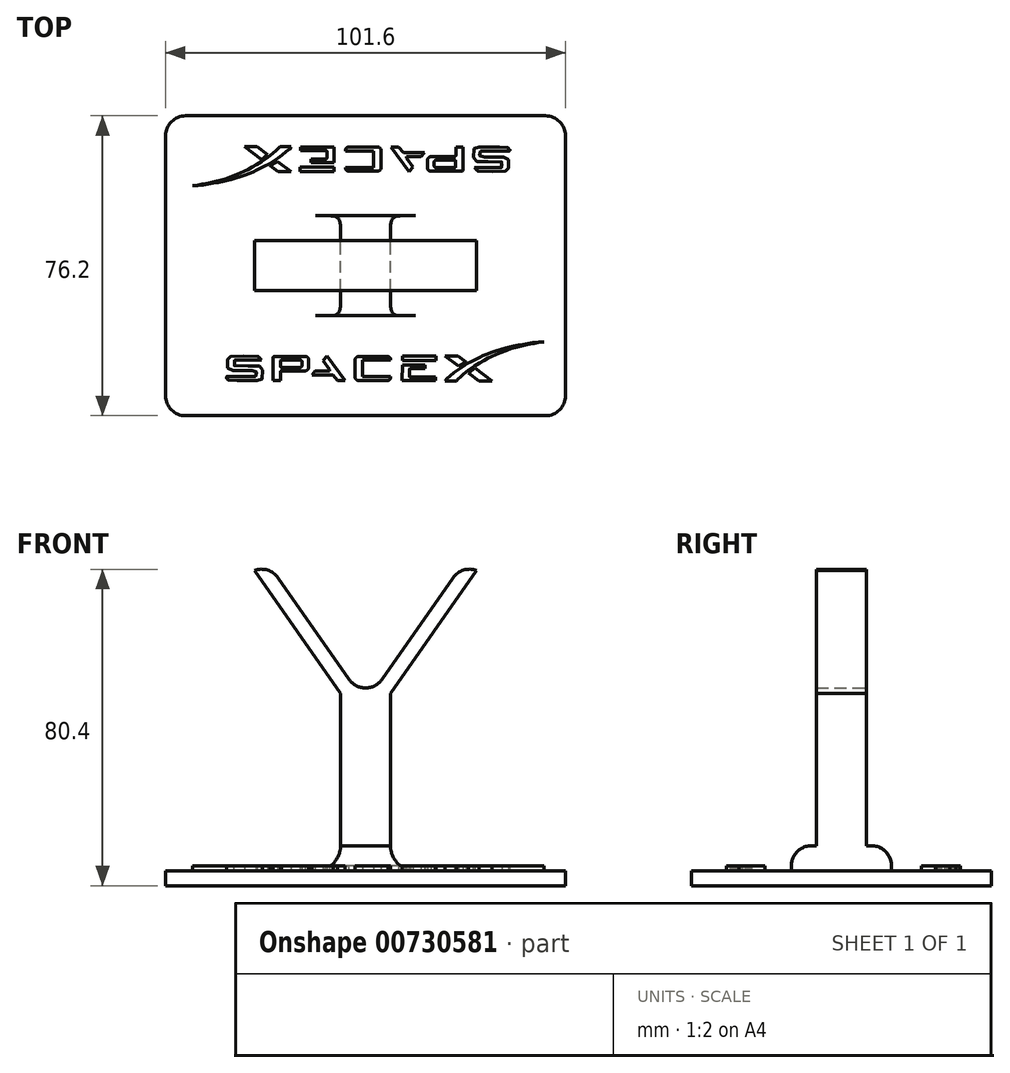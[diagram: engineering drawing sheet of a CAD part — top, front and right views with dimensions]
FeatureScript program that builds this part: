
annotation { "Feature Type Name" : "Feature", "Feature Type Description" : "" }
export const myFeature = defineFeature(function(context is Context, id is Id, definition is map)
    precondition{}
    {
        {
            var Q0;
            Q0=qCreatedBy(makeId("Front.planeOp"),FACE);
            var sketch = newSketch(context, id + "F0", { "sketchPlane" : qUnion([Q0])});
            skLineSegment(sketch, "E0.left", {"start": v(-20.93, 31.6) * mm, "end": v(-20.93, 73.8) * mm});
            skLineSegment(sketch, "E0.right", {"start": v(-33.63, 31.6) * mm, "end": v(-33.63, 73.8) * mm});
            skArc(sketch, "E1.filletArc", {"start": v(-39.98, 25.26) * mm, "mid": v(-35.5, 27.12) * mm, "end": v(-33.63, 31.6) * mm});
            skLineSegment(sketch, "E2", {"start": v(23.52, 25.26) * mm, "end": v(-14.58, 25.26) * mm});
            skArc(sketch, "E3.filletArc", {"start": v(-20.93, 31.6) * mm, "mid": v(-19.07, 27.12) * mm, "end": v(-14.58, 25.26) * mm});
            skLineSegment(sketch, "E4", {"start": v(-33.63, 70.32) * mm, "end": v(-55.49, 101.53) * mm});
            skLineSegment(sketch, "E5", {"start": v(-78.08, 21.45) * mm, "end": v(-78.08, 25.26) * mm});
            skLineSegment(sketch, "E6", {"start": v(23.52, 21.45) * mm, "end": v(23.52, 25.26) * mm});
            skLineSegment(sketch, "E7", {"start": v(-78.08, 25.26) * mm, "end": v(-39.98, 25.26) * mm});
            skLineSegment(sketch, "E8", {"start": v(-78.08, 21.45) * mm, "end": v(23.52, 21.45) * mm});
            skLineSegment(sketch, "E9", {"start": v(-55.49, 101.53) * mm, "end": v(-52.37, 103.71) * mm});
            skLineSegment(sketch, "E10", {"start": v(-52.37, 103.71) * mm, "end": v(-27.28, 67.9) * mm});
            skLineSegment(sketch, "E11.MirrorCS", {"start": v(-2.2, 103.71) * mm, "end": v(-27.28, 67.9) * mm});
            skLineSegment(sketch, "E12.MirrorCS", {"start": v(0.92, 101.53) * mm, "end": v(-2.2, 103.71) * mm});
            skLineSegment(sketch, "E13.MirrorCS", {"start": v(-20.93, 70.32) * mm, "end": v(0.92, 101.53) * mm});
            skLineSegment(sketch, "E14", {"start": v(-33.63, 62.87) * mm, "end": v(-20.93, 62.87) * mm});
            skLineSegment(sketch, "E15", {"start": v(-39.98, 25.26) * mm, "end": v(-14.58, 25.26) * mm});
            skLineSegment(sketch, "E16", {"start": v(-33.63, 31.6) * mm, "end": v(-20.93, 31.6) * mm});
            skSolve(sketch);
        }
        {
            var Q0;
            {var subQ1=sQuery(id+"F0.wireOp",EDGE,"E5");Q0=makeQuery(id+"F0.imprint","IMPRINT",FACE,{"disambiguationData":[TD([[makeQuery(id+"F0.imprint","IMPRINT",EDGE,{"derivedFrom":subQ1}),-1.0]])]});}
            var Q1;
            {var subQ6=sQuery(id+"F0.wireOp",EDGE,"E2");Q1=makeQuery(id+"F0.imprint","IMPRINT",FACE,{"disambiguationData":[TD([[makeQuery(id+"F0.imprint","IMPRINT",EDGE,{"derivedFrom":subQ6}),1.0]])]});}
            extrude(context, id + "F1", {"entities" : qUnion([Q0, Q1]), "depth" : 76.2 * mm, "offsetDistance" : 25.4 * mm, "symmetric" : true});
        }
        {
            var Q0;
            Q0=makeQuery(id+"F0.imprint","IMPRINT",FACE,{"disambiguationData":[TD([[makeQuery(id+"F0.imprint","IMPRINT",EDGE,{"derivedFrom":sQuery(id+"F0.wireOp",EDGE,"E1.filletArc")}),-1.0]])]});
            extrude(context, id + "F2", {"entities" : qUnion([Q0]), "operationType" : NewBodyOperationType.ADD, "depth" : 25.4 * mm, "offsetDistance" : 25.4 * mm, "symmetric" : true});
        }
        {
            var Q0;
            {var subQ2=sQuery(id+"F0.wireOp",EDGE,"E14");Q0=makeQuery(id+"F0.imprint","IMPRINT",FACE,{"disambiguationData":[TD([[makeQuery(id+"F0.imprint","IMPRINT",EDGE,{"derivedFrom":subQ2}),-1.0]])]});}
            var Q1;
            {var subQ3=sQuery(id+"F0.wireOp",EDGE,"E4");Q1=makeQuery(id+"F0.imprint","IMPRINT",FACE,{"disambiguationData":[TD([[makeQuery(id+"F0.imprint","IMPRINT",EDGE,{"derivedFrom":subQ3}),-1.0]])]});}
            extrude(context, id + "F3", {"entities" : qUnion([Q0, Q1]), "operationType" : NewBodyOperationType.ADD, "depth" : 12.7 * mm, "offsetDistance" : 25.4 * mm, "symmetric" : true});
        }
        {
            var Q0;
            Q0=makeQuery(id+"F2.opExtrude","CAP_EDGE",EDGE,{"disambiguationData":[OSD([sQuery(id+"F0.wireOp",EDGE,"E16")])],"isStart":false});
            var Q1;
            Q1=makeQuery(id+"F2.opExtrude","CAP_EDGE",EDGE,{"disambiguationData":[OSD([sQuery(id+"F0.wireOp",EDGE,"E16")])],"isStart":true});
            fillet(context, id + "F4", {"entities" : qUnion([Q0, Q1]), "radius" : 5.08 * mm, "tangentPropagation" : true, "allowEdgeOverflow" : false});
        }
        {
            var Q0;
            Q0=makeQuery(id+"F1.opExtrude","CAP_EDGE",EDGE,{"disambiguationData":[OSD([sQuery(id+"F0.wireOp",EDGE,"E6")])],"isStart":false});
            var Q1;
            Q1=makeQuery(id+"F1.opExtrude","CAP_EDGE",EDGE,{"disambiguationData":[OSD([sQuery(id+"F0.wireOp",EDGE,"E6")])],"isStart":true});
            var Q2;
            Q2=makeQuery(id+"F1.opExtrude","CAP_EDGE",EDGE,{"disambiguationData":[OSD([sQuery(id+"F0.wireOp",EDGE,"E5")])],"isStart":true});
            var Q3;
            Q3=makeQuery(id+"F1.opExtrude","CAP_EDGE",EDGE,{"disambiguationData":[OSD([sQuery(id+"F0.wireOp",EDGE,"E5")])],"isStart":false});
            var Q4;
            Q4=makeQuery(id+"F3.opExtrude","SWEPT_EDGE",EDGE,{"disambiguationData":[OSD([sQuery(id+"F0.wireOp",EDGE,"E11.MirrorCS"),sQuery(id+"F0.wireOp",EDGE,"E12.MirrorCS")])]});
            var Q5;
            Q5=makeQuery(id+"F3.opExtrude","SWEPT_EDGE",EDGE,{"disambiguationData":[OSD([sQuery(id+"F0.wireOp",EDGE,"E9"),sQuery(id+"F0.wireOp",EDGE,"E10")])]});
            var Q6;
            Q6=makeQuery(id+"F3.opExtrude","SWEPT_EDGE",EDGE,{"disambiguationData":[OSD([sQuery(id+"F0.wireOp",EDGE,"E10"),sQuery(id+"F0.wireOp",EDGE,"E11.MirrorCS")])]});
            fillet(context, id + "F5", {"entities" : qUnion([Q0, Q1, Q2, Q3, Q4, Q5, Q6]), "radius" : 5.08 * mm, "tangentPropagation" : true, "allowEdgeOverflow" : false});
        }
        {
            var Q0;
            Q0=makeQuery(id+"F1.opExtrude","SWEPT_BODY",BODY,{"disambiguationData":[OSD([sQuery(id+"F0.wireOp",EDGE,"E2"),sQuery(id+"F0.wireOp",EDGE,"E5"),sQuery(id+"F0.wireOp",EDGE,"E6"),sQuery(id+"F0.wireOp",EDGE,"E7"),sQuery(id+"F0.wireOp",EDGE,"E8"),sQuery(id+"F0.wireOp",EDGE,"E15")])]});
            transform(context, id + "F6", {"entities" : qUnion([Q0]), "transformType" : TransformType.TRANSLATION_3D, "dx" : 0 * mm, "dy" : 0 * mm, "dz" : -22.1 * mm, "makeCopy" : false});
        }
        {
            var Q0;
            Q0=qCreatedBy(makeId("Top.planeOp"),FACE);
            var sketch = newSketch(context, id + "F7", { "sketchPlane" : qUnion([Q0])});
            skFitSpline(sketch, "E17", {"points": [v(-53.7, -23.92) * mm, v(-53.67, -23.65) * mm, v(-54.32, -23.13) * mm, v(-55.17, -23) * mm, v(-61.33, -23.02) * mm, v(-61.6, -23.06) * mm, v(-61.93, -23.15) * mm, v(-62.22, -23.56) * mm, v(-62.38, -24.03) * mm, v(-62.32, -25.77) * mm, v(-62.18, -26.17) * mm, v(-61.56, -26.5) * mm, v(-59.98, -26.56) * mm, v(-57.92, -26.56) * mm, v(-56.25, -26.56) * mm, v(-55.43, -26.6) * mm, v(-55.05, -26.71) * mm, v(-55, -27.47) * mm, v(-55, -28) * mm, v(-55.23, -28.12) * mm, v(-55.77, -28.13) * mm, v(-62.38, -28.13) * mm, v(-62.6, -28.18) * mm, v(-62.64, -28.45) * mm, v(-62.48, -28.76) * mm, v(-61.97, -29.1) * mm, v(-61.31, -29.16) * mm, v(-54.45, -29.16) * mm, v(-54.07, -29.11) * mm, v(-53.64, -28.84) * mm, v(-53.44, -28.23) * mm, v(-53.44, -26.31) * mm, v(-53.63, -25.89) * mm, v(-54.23, -25.5) * mm, v(-55.29, -25.42) * mm, v(-60.36, -25.4) * mm, v(-60.65, -25.3) * mm, v(-60.72, -24.19) * mm, v(-60.45, -24) * mm, v(-54.19, -23.94) * mm, v(-53.88, -23.9) * mm, v(-53.7, -23.92) * mm]});
            skLineSegment(sketch, "E18", {"start": v(-50.52, -23.04) * mm, "end": v(-42.6, -23.04) * mm});
            skLineSegment(sketch, "E19", {"start": v(-48.66, -23.95) * mm, "end": v(-43.86, -23.95) * mm});
            skLineSegment(sketch, "E20", {"start": v(-43.44, -24.28) * mm, "end": v(-43.44, -25.47) * mm});
            skLineSegment(sketch, "E21", {"start": v(-48.68, -25.82) * mm, "end": v(-43.94, -25.82) * mm});
            skLineSegment(sketch, "E22", {"start": v(-48.88, -24.14) * mm, "end": v(-48.88, -25.62) * mm});
            skLineSegment(sketch, "E23", {"start": v(-50.74, -23.29) * mm, "end": v(-50.74, -29.17) * mm});
            skLineSegment(sketch, "E24", {"start": v(-50.74, -29.17) * mm, "end": v(-48.91, -29.17) * mm});
            skLineSegment(sketch, "E25", {"start": v(-48.91, -29.17) * mm, "end": v(-48.91, -26.97) * mm});
            skLineSegment(sketch, "E26", {"start": v(-48.62, -26.7) * mm, "end": v(-42.66, -26.7) * mm});
            skLineSegment(sketch, "E27", {"start": v(-41.74, -23.79) * mm, "end": v(-41.74, -25.97) * mm});
            skFitSpline(sketch, "E28", {"points": [v(-42.6, -23.04) * mm, v(-42.1, -23.18) * mm, v(-41.74, -23.79) * mm], "startDerivative": vector(1.29, -0.1) * mm, "endDerivative": vector(0.06, -1.49) * mm});
            skArc(sketch, "E29", {"start": v(-48.66, -23.95) * mm, "mid": v(-48.8, -24) * mm, "end": v(-48.88, -24.14) * mm});
            skArc(sketch, "E30", {"start": v(-43.44, -24.28) * mm, "mid": v(-43.6, -24.05) * mm, "end": v(-43.86, -23.95) * mm});
            skArc(sketch, "E31", {"start": v(-43.94, -25.82) * mm, "mid": v(-43.64, -25.72) * mm, "end": v(-43.44, -25.47) * mm});
            skArc(sketch, "E32", {"start": v(-48.88, -25.62) * mm, "mid": v(-48.82, -25.76) * mm, "end": v(-48.68, -25.82) * mm});
            skArc(sketch, "E33", {"start": v(-48.62, -26.7) * mm, "mid": v(-48.83, -26.78) * mm, "end": v(-48.91, -26.97) * mm});
            skArc(sketch, "E34", {"start": v(-50.52, -23.04) * mm, "mid": v(-50.68, -23.12) * mm, "end": v(-50.74, -23.29) * mm});
            skArc(sketch, "E35", {"start": v(-42.66, -26.7) * mm, "mid": v(-42.07, -26.5) * mm, "end": v(-41.74, -25.97) * mm});
            skLineSegment(sketch, "E36", {"start": v(-40.1, -26.79) * mm, "end": v(-36.45, -26.79) * mm});
            skLineSegment(sketch, "E37", {"start": v(-40.93, -27.8) * mm, "end": v(-35.58, -27.8) * mm});
            skLineSegment(sketch, "E38", {"start": v(-34.41, -29.2) * mm, "end": v(-32.43, -29.2) * mm});
            skLineSegment(sketch, "E39", {"start": v(-36.45, -26.79) * mm, "end": v(-36.45, -26.32) * mm});
            skLineSegment(sketch, "E40", {"start": v(-36.45, -26.32) * mm, "end": v(-38.08, -24.1) * mm});
            skLineSegment(sketch, "E41", {"start": v(-38.08, -24.1) * mm, "end": v(-37.07, -22.88) * mm});
            skLineSegment(sketch, "E42", {"start": v(-37.07, -22.88) * mm, "end": v(-32.43, -29.2) * mm});
            skLineSegment(sketch, "E43", {"start": v(-40.93, -27.8) * mm, "end": v(-40.1, -26.79) * mm});
            skLineSegment(sketch, "E44", {"start": v(-35.58, -27.8) * mm, "end": v(-34.41, -29.2) * mm});
            skLineSegment(sketch, "E45", {"start": v(-28.05, -23.98) * mm, "end": v(-28.05, -28.08) * mm});
            skLineSegment(sketch, "E46", {"start": v(-28.05, -28.08) * mm, "end": v(-20.92, -28.08) * mm});
            skLineSegment(sketch, "E47", {"start": v(-28.05, -23.98) * mm, "end": v(-20.93, -23.98) * mm});
            skLineSegment(sketch, "E48", {"start": v(-29.95, -23.98) * mm, "end": v(-29.95, -28.17) * mm});
            skLineSegment(sketch, "E49", {"start": v(-29.03, -23.05) * mm, "end": v(-21.68, -23.05) * mm});
            skLineSegment(sketch, "E50", {"start": v(-28.99, -29.18) * mm, "end": v(-21.6, -29.18) * mm});
            skArc(sketch, "E51", {"start": v(-29.03, -23.05) * mm, "mid": v(-29.68, -23.32) * mm, "end": v(-29.95, -23.98) * mm});
            skArc(sketch, "E52", {"start": v(-20.93, -23.98) * mm, "mid": v(-21.08, -23.34) * mm, "end": v(-21.68, -23.05) * mm});
            skArc(sketch, "E53", {"start": v(-21.6, -29.18) * mm, "mid": v(-21.04, -28.77) * mm, "end": v(-20.92, -28.08) * mm});
            skArc(sketch, "E54", {"start": v(-29.95, -28.17) * mm, "mid": v(-29.68, -28.88) * mm, "end": v(-28.99, -29.18) * mm});
            skLineSegment(sketch, "E55", {"start": v(-17.93, -22.97) * mm, "end": v(-17.93, -24.06) * mm});
            skLineSegment(sketch, "E56", {"start": v(-17.93, -24.06) * mm, "end": v(-9.36, -24.06) * mm});
            skLineSegment(sketch, "E57", {"start": v(-9.36, -24.06) * mm, "end": v(-9.36, -23) * mm});
            skLineSegment(sketch, "E58", {"start": v(-9.36, -23) * mm, "end": v(-17.93, -22.97) * mm});
            skLineSegment(sketch, "E59", {"start": v(-17.93, -25.16) * mm, "end": v(-12.2, -25.16) * mm});
            skLineSegment(sketch, "E60", {"start": v(-12.2, -25.16) * mm, "end": v(-12.2, -26.1) * mm});
            skLineSegment(sketch, "E61", {"start": v(-12.2, -26.1) * mm, "end": v(-15.84, -26.1) * mm});
            skLineSegment(sketch, "E62", {"start": v(-16.16, -26.36) * mm, "end": v(-16.16, -28.1) * mm});
            skLineSegment(sketch, "E63", {"start": v(-15.85, -28.28) * mm, "end": v(-9.49, -28.28) * mm});
            skLineSegment(sketch, "E64", {"start": v(-9.49, -28.28) * mm, "end": v(-9.49, -29.2) * mm});
            skLineSegment(sketch, "E65", {"start": v(-9.49, -29.2) * mm, "end": v(-17.95, -29.2) * mm});
            skLineSegment(sketch, "E66", {"start": v(-17.95, -29.2) * mm, "end": v(-17.93, -25.16) * mm});
            skArc(sketch, "E67", {"start": v(-15.84, -26.1) * mm, "mid": v(-16.05, -26.17) * mm, "end": v(-16.16, -26.36) * mm});
            skArc(sketch, "E68", {"start": v(-16.16, -28.1) * mm, "mid": v(-16.04, -28.25) * mm, "end": v(-15.85, -28.28) * mm});
            skLineSegment(sketch, "E69", {"start": v(-3.63, -25.47) * mm, "end": v(-7.06, -22.9) * mm});
            skLineSegment(sketch, "E70", {"start": v(-7.06, -22.9) * mm, "end": v(-3.82, -22.9) * mm});
            skLineSegment(sketch, "E71", {"start": v(-3.82, -22.9) * mm, "end": v(-1.73, -24.46) * mm});
            skLineSegment(sketch, "E72", {"start": v(-1.73, -24.46) * mm, "end": v(-3.63, -25.47) * mm});
            skLineSegment(sketch, "E73", {"start": v(-1.12, -27.26) * mm, "end": v(1.55, -29.22) * mm});
            skLineSegment(sketch, "E74", {"start": v(1.55, -29.22) * mm, "end": v(4.8, -29.22) * mm});
            skLineSegment(sketch, "E75", {"start": v(4.8, -29.22) * mm, "end": v(0.47, -26.03) * mm});
            skLineSegment(sketch, "E76", {"start": v(0.47, -26.03) * mm, "end": v(-1.12, -27.26) * mm});
            skFitSpline(sketch, "E77", {"points": [v(-4.23, -29.23) * mm, v(-3.52, -28.52) * mm, v(-2.4, -27.5) * mm, v(0.11, -25.65) * mm, v(3.4, -23.71) * mm, v(5.5, -22.67) * mm, v(9.22, -21.24) * mm, v(11.62, -20.56) * mm, v(13.9, -20.02) * mm, v(15.25, -19.77) * mm, v(17.22, -19.44) * mm, v(18.02, -19.37) * mm], "startDerivative": vector(10.87, 11.15) * mm, "endDerivative": vector(12.33, 0.65) * mm});
            skLineSegment(sketch, "E78", {"start": v(-4.23, -29.23) * mm, "end": v(-7.08, -29.23) * mm});
            skFitSpline(sketch, "E79", {"points": [v(-7.08, -29.23) * mm, v(-6.81, -28.85) * mm, v(-6.22, -28.29) * mm, v(-5.06, -27.3) * mm, v(-3.56, -26.22) * mm, v(-2.03, -25.2) * mm, v(-0.72, -24.47) * mm, v(0.48, -23.87) * mm, v(1.64, -23.27) * mm, v(2.58, -22.85) * mm, v(3.7, -22.38) * mm, v(4.77, -21.96) * mm, v(6.18, -21.52) * mm, v(7.73, -21.07) * mm, v(8.94, -20.77) * mm, v(10.06, -20.5) * mm, v(11.42, -20.22) * mm, v(12.81, -19.93) * mm, v(14.55, -19.66) * mm, v(16.14, -19.45) * mm, v(18.02, -19.37) * mm], "startDerivative": vector(8, 12.9) * mm, "endDerivative": vector(32.76, 0.76) * mm});
            skFitSpline(sketch, "E80", {"points": [v(0.43, 24.93) * mm, v(0.4, 24.65) * mm, v(1.05, 24.14) * mm, v(1.9, 24) * mm, v(8.06, 24.02) * mm, v(8.34, 24.07) * mm, v(8.66, 24.15) * mm, v(8.95, 24.56) * mm, v(9.11, 25.03) * mm, v(9.05, 26.78) * mm, v(8.9, 27.17) * mm, v(8.3, 27.51) * mm, v(6.7, 27.57) * mm, v(4.66, 27.57) * mm, v(2.98, 27.57) * mm, v(2.16, 27.6) * mm, v(1.78, 27.72) * mm, v(1.72, 28.48) * mm, v(1.72, 29) * mm, v(1.96, 29.12) * mm, v(2.5, 29.14) * mm, v(9.11, 29.14) * mm, v(9.33, 29.18) * mm, v(9.38, 29.46) * mm, v(9.22, 29.77) * mm, v(8.7, 30.1) * mm, v(8.04, 30.16) * mm, v(1.18, 30.16) * mm, v(0.8, 30.12) * mm, v(0.37, 29.84) * mm, v(0.17, 29.24) * mm, v(0.17, 27.32) * mm, v(0.36, 26.9) * mm, v(0.96, 26.5) * mm, v(2.02, 26.43) * mm, v(7.09, 26.41) * mm, v(7.38, 26.3) * mm, v(7.46, 25.2) * mm, v(7.18, 25) * mm, v(0.92, 24.95) * mm, v(0.6, 24.92) * mm, v(0.43, 24.93) * mm]});
            skLineSegment(sketch, "E81", {"start": v(-2.75, 24.05) * mm, "end": v(-10.67, 24.05) * mm});
            skLineSegment(sketch, "E82", {"start": v(-4.61, 24.96) * mm, "end": v(-9.4, 24.96) * mm});
            skLineSegment(sketch, "E83", {"start": v(-9.82, 25.29) * mm, "end": v(-9.82, 26.48) * mm});
            skLineSegment(sketch, "E84", {"start": v(-4.6, 26.82) * mm, "end": v(-9.33, 26.82) * mm});
            skLineSegment(sketch, "E85", {"start": v(-4.39, 25.15) * mm, "end": v(-4.39, 26.62) * mm});
            skLineSegment(sketch, "E86", {"start": v(-2.53, 24.3) * mm, "end": v(-2.53, 30.18) * mm});
            skLineSegment(sketch, "E87", {"start": v(-2.53, 30.18) * mm, "end": v(-4.36, 30.18) * mm});
            skLineSegment(sketch, "E88", {"start": v(-4.36, 30.18) * mm, "end": v(-4.36, 27.98) * mm});
            skLineSegment(sketch, "E89", {"start": v(-4.64, 27.71) * mm, "end": v(-10.6, 27.71) * mm});
            skLineSegment(sketch, "E90", {"start": v(-11.52, 24.8) * mm, "end": v(-11.52, 26.98) * mm});
            skFitSpline(sketch, "E91", {"points": [v(-10.67, 24.05) * mm, v(-11.17, 24.19) * mm, v(-11.52, 24.8) * mm], "startDerivative": vector(-1.29, 0.1) * mm, "endDerivative": vector(-0.06, 1.49) * mm});
            skArc(sketch, "E92", {"start": v(-4.61, 24.96) * mm, "mid": v(-4.46, 25.01) * mm, "end": v(-4.39, 25.15) * mm});
            skArc(sketch, "E93", {"start": v(-9.82, 25.29) * mm, "mid": v(-9.67, 25.05) * mm, "end": v(-9.4, 24.96) * mm});
            skArc(sketch, "E94", {"start": v(-9.33, 26.82) * mm, "mid": v(-9.63, 26.73) * mm, "end": v(-9.82, 26.48) * mm});
            skArc(sketch, "E95", {"start": v(-4.39, 26.62) * mm, "mid": v(-4.45, 26.77) * mm, "end": v(-4.6, 26.82) * mm});
            skArc(sketch, "E96", {"start": v(-4.64, 27.71) * mm, "mid": v(-4.44, 27.78) * mm, "end": v(-4.36, 27.98) * mm});
            skArc(sketch, "E97", {"start": v(-2.75, 24.05) * mm, "mid": v(-2.58, 24.12) * mm, "end": v(-2.53, 24.3) * mm});
            skArc(sketch, "E98", {"start": v(-10.6, 27.71) * mm, "mid": v(-11.2, 27.5) * mm, "end": v(-11.52, 26.98) * mm});
            skLineSegment(sketch, "E99", {"start": v(-13.16, 27.8) * mm, "end": v(-16.82, 27.8) * mm});
            skLineSegment(sketch, "E100", {"start": v(-12.34, 28.8) * mm, "end": v(-17.69, 28.8) * mm});
            skLineSegment(sketch, "E101", {"start": v(-18.85, 30.2) * mm, "end": v(-20.84, 30.2) * mm});
            skLineSegment(sketch, "E102", {"start": v(-16.82, 27.8) * mm, "end": v(-16.82, 27.33) * mm});
            skLineSegment(sketch, "E103", {"start": v(-16.82, 27.33) * mm, "end": v(-15.19, 25.1) * mm});
            skLineSegment(sketch, "E104", {"start": v(-15.19, 25.1) * mm, "end": v(-16.2, 23.89) * mm});
            skLineSegment(sketch, "E105", {"start": v(-16.2, 23.89) * mm, "end": v(-20.84, 30.2) * mm});
            skLineSegment(sketch, "E106", {"start": v(-12.34, 28.8) * mm, "end": v(-13.16, 27.8) * mm});
            skLineSegment(sketch, "E107", {"start": v(-17.69, 28.8) * mm, "end": v(-18.85, 30.2) * mm});
            skLineSegment(sketch, "E108", {"start": v(-25.21, 24.98) * mm, "end": v(-25.21, 29.09) * mm});
            skLineSegment(sketch, "E109", {"start": v(-25.21, 29.09) * mm, "end": v(-32.35, 29.09) * mm});
            skLineSegment(sketch, "E110", {"start": v(-25.21, 24.98) * mm, "end": v(-32.34, 24.98) * mm});
            skLineSegment(sketch, "E111", {"start": v(-23.32, 24.98) * mm, "end": v(-23.32, 29.18) * mm});
            skLineSegment(sketch, "E112", {"start": v(-24.24, 24.06) * mm, "end": v(-31.6, 24.06) * mm});
            skLineSegment(sketch, "E113", {"start": v(-24.28, 30.19) * mm, "end": v(-31.66, 30.19) * mm});
            skArc(sketch, "E114", {"start": v(-24.24, 24.06) * mm, "mid": v(-23.59, 24.33) * mm, "end": v(-23.32, 24.98) * mm});
            skArc(sketch, "E115", {"start": v(-32.34, 24.98) * mm, "mid": v(-32.18, 24.34) * mm, "end": v(-31.6, 24.06) * mm});
            skArc(sketch, "E116", {"start": v(-31.66, 30.19) * mm, "mid": v(-32.23, 29.78) * mm, "end": v(-32.35, 29.09) * mm});
            skArc(sketch, "E117", {"start": v(-23.32, 29.18) * mm, "mid": v(-23.58, 29.89) * mm, "end": v(-24.28, 30.19) * mm});
            skLineSegment(sketch, "E118", {"start": v(-35.34, 23.98) * mm, "end": v(-35.34, 25.07) * mm});
            skLineSegment(sketch, "E119", {"start": v(-35.34, 25.07) * mm, "end": v(-43.91, 25.07) * mm});
            skLineSegment(sketch, "E120", {"start": v(-43.91, 25.07) * mm, "end": v(-43.91, 24) * mm});
            skLineSegment(sketch, "E121", {"start": v(-43.91, 24) * mm, "end": v(-35.34, 23.98) * mm});
            skLineSegment(sketch, "E122", {"start": v(-35.34, 26.16) * mm, "end": v(-41.07, 26.16) * mm});
            skLineSegment(sketch, "E123", {"start": v(-41.07, 26.16) * mm, "end": v(-41.07, 27.1) * mm});
            skLineSegment(sketch, "E124", {"start": v(-41.07, 27.1) * mm, "end": v(-37.43, 27.1) * mm});
            skLineSegment(sketch, "E125", {"start": v(-37.1, 27.36) * mm, "end": v(-37.1, 29.1) * mm});
            skLineSegment(sketch, "E126", {"start": v(-37.42, 29.28) * mm, "end": v(-43.78, 29.28) * mm});
            skLineSegment(sketch, "E127", {"start": v(-43.78, 29.28) * mm, "end": v(-43.78, 30.22) * mm});
            skLineSegment(sketch, "E128", {"start": v(-43.78, 30.22) * mm, "end": v(-35.32, 30.22) * mm});
            skLineSegment(sketch, "E129", {"start": v(-35.32, 30.22) * mm, "end": v(-35.34, 26.16) * mm});
            skArc(sketch, "E130", {"start": v(-37.43, 27.1) * mm, "mid": v(-37.22, 27.18) * mm, "end": v(-37.1, 27.36) * mm});
            skArc(sketch, "E131", {"start": v(-37.1, 29.1) * mm, "mid": v(-37.23, 29.26) * mm, "end": v(-37.42, 29.28) * mm});
            skLineSegment(sketch, "E132", {"start": v(-49.64, 26.48) * mm, "end": v(-46.2, 23.9) * mm});
            skLineSegment(sketch, "E133", {"start": v(-46.2, 23.9) * mm, "end": v(-49.45, 23.9) * mm});
            skLineSegment(sketch, "E134", {"start": v(-49.45, 23.9) * mm, "end": v(-51.54, 25.46) * mm});
            skLineSegment(sketch, "E135", {"start": v(-51.54, 25.46) * mm, "end": v(-49.64, 26.48) * mm});
            skLineSegment(sketch, "E136", {"start": v(-52.15, 28.27) * mm, "end": v(-54.82, 30.23) * mm});
            skLineSegment(sketch, "E137", {"start": v(-54.82, 30.23) * mm, "end": v(-58.07, 30.23) * mm});
            skLineSegment(sketch, "E138", {"start": v(-58.07, 30.23) * mm, "end": v(-53.74, 27.03) * mm});
            skLineSegment(sketch, "E139", {"start": v(-53.74, 27.03) * mm, "end": v(-52.15, 28.27) * mm});
            skFitSpline(sketch, "E140", {"points": [v(-49.04, 30.24) * mm, v(-49.75, 29.53) * mm, v(-50.87, 28.51) * mm, v(-53.38, 26.66) * mm, v(-56.68, 24.72) * mm, v(-58.77, 23.67) * mm, v(-62.48, 22.24) * mm, v(-64.89, 21.56) * mm, v(-67.17, 21.02) * mm, v(-68.52, 20.78) * mm, v(-70.49, 20.45) * mm, v(-71.29, 20.38) * mm], "startDerivative": vector(-10.87, -11.15) * mm, "endDerivative": vector(-12.33, -0.65) * mm});
            skLineSegment(sketch, "E141", {"start": v(-49.04, 30.24) * mm, "end": v(-46.19, 30.24) * mm});
            skFitSpline(sketch, "E142", {"points": [v(-46.19, 30.24) * mm, v(-46.46, 29.86) * mm, v(-47.05, 29.3) * mm, v(-48.2, 28.31) * mm, v(-49.7, 27.22) * mm, v(-51.24, 26.21) * mm, v(-52.55, 25.47) * mm, v(-53.74, 24.88) * mm, v(-54.91, 24.28) * mm, v(-55.84, 23.86) * mm, v(-56.96, 23.39) * mm, v(-58.04, 22.97) * mm, v(-59.44, 22.53) * mm, v(-61, 22.07) * mm, v(-62.2, 21.78) * mm, v(-63.33, 21.51) * mm, v(-64.68, 21.23) * mm, v(-66.08, 20.94) * mm, v(-67.81, 20.67) * mm, v(-69.4, 20.46) * mm, v(-71.29, 20.38) * mm], "startDerivative": vector(-8, -12.9) * mm, "endDerivative": vector(-32.76, -0.76) * mm});
            skSolve(sketch);
        }
        {
            var Q0;
            Q0 = qSketchRegion(id + "F7", true);
            extrude(context, id + "F8", {"entities" : qUnion([Q0]), "operationType" : NewBodyOperationType.ADD, "depth" : 4.32 * mm, "offsetDistance" : 25.4 * mm});
        }
    });
